# Revit family: Sensor_Dimmer_and_Switch-Lutron-Maestro_MS
name_source: partatom
category: Lighting Devices
revit_build: Autodesk Revit 2018 (Build: 20170223_1515(x64)
units: mm (PartAtom-declared; Revit-internal decimal feet)

## family parameters
Cut with Voids When Loaded = No
Host = Face
Maintain Annotation Orientation = No
OmniClass Number = 23.85.80.11.27
OmniClass Title = Lighting Controls
Part Type = Normal
Room Calculation Point = No
Round Connector Dimension = Use Diameter
Shared = No

## types (3) — shared parameters
Apparent Load = 0 VA
Assembly Code = D5020
Default Elevation = 0' - 0"
Finish = Plastic - Lutron - Almond - Matte
Instruction Sheet Link = https://www.lutron.com
Keynote = Division 11
Manufacturer = Lutron Electronics Co., Inc
Manufacturer Fax Number = 610-282-1243
Maximum Operating Temperature = 104 °F
Minimum Operating Temperature = 32 °F
Number of Poles = 1
Operating Voltage = 120/277 V
Overall Depth = 0' - 0 5/16"
Overall Height = 0' - 4 11/16"
Overall Width = 0' - 2 15/16"
Performance URL = http://www.lutron.com
Power Factor = 1
Product Documentation Link = https://www.lutron.com
Product Name = Maestro 0–10 V Dimmer Sensor
Product Page URL = https://www.lutron.com
Series = Vive
Type Comments = -
URL = http://www.lutron.com
Version = 2018 - v1.0a
Video Link = https://www.youtube.com
Voltage = 0 V
Warranty URL = http://www.lutron.com
zero-valued in all types: Cost

## per-type parameters (varying)
| type | Description | Load Classification |
| MS-Z101-XX | Occupancy / vacancy Single-pole/multi-location | Other |
| MS-Z101-V-XX | Vacancy Single-pole/ multi-location | Other |
| WMS-Z101-XX | Occupancy / vacancy Single-pole/multi-location | Lighting |

note: column(s) folded — value = type name in every type: Model

## geometry (parser evidence)
native form markers: Blend x4, Sweep x3
no freeform markers — native parametric forms only
